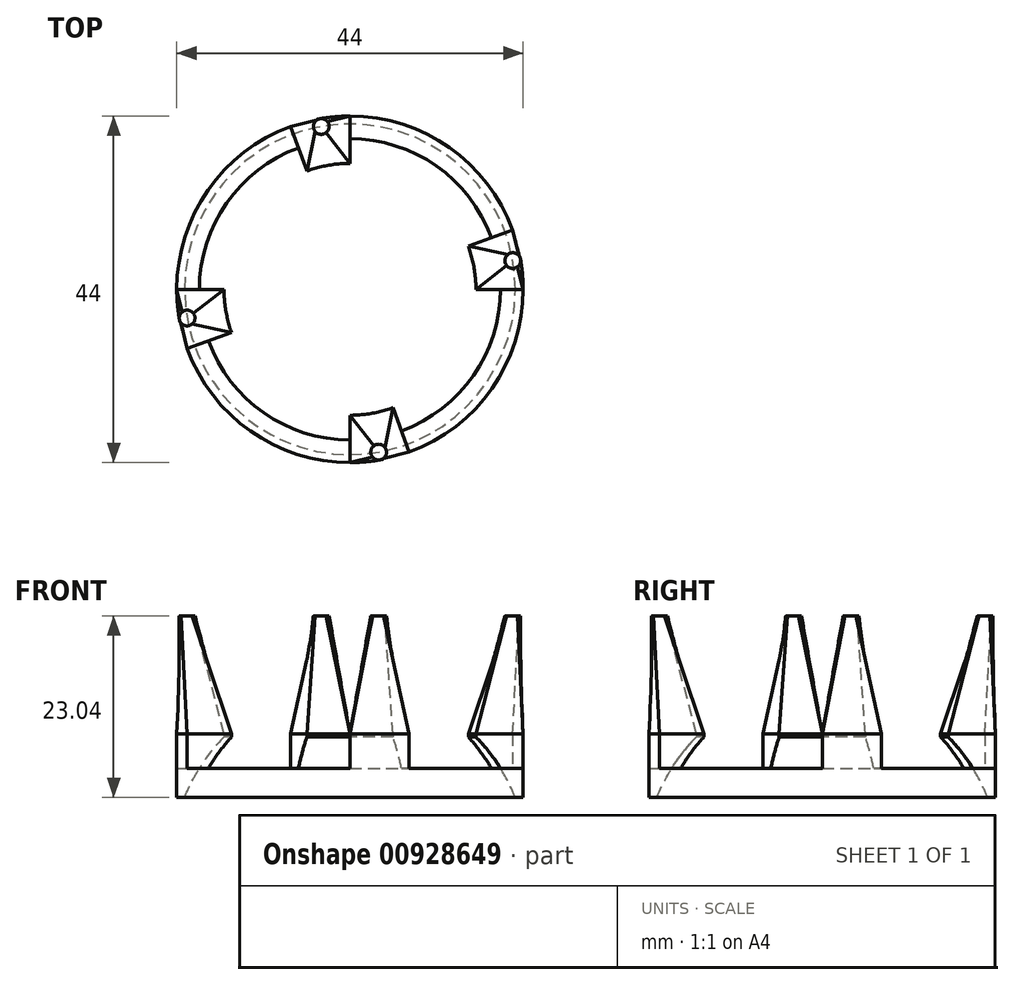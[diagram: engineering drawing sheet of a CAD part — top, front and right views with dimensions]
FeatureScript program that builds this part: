
annotation { "Feature Type Name" : "Feature", "Feature Type Description" : "" }
export const myFeature = defineFeature(function(context is Context, id is Id, definition is map)
    precondition{}
    {
        {
            var Q0;
            Q0=qCreatedBy(makeId("Front.planeOp"),FACE);
            var sketch = newSketch(context, id + "F0", { "sketchPlane" : qUnion([Q0])});
            skLineSegment(sketch, "E0", {"start": v(0, 0) * mm, "end": v(0, 52.54) * mm, "construction": true});
            skLineSegment(sketch, "E1.bottom", {"start": v(16, 0) * mm, "end": v(22, 0) * mm});
            skLineSegment(sketch, "E1.top", {"start": v(16, -8.04) * mm, "end": v(21, -8.04) * mm, "construction": true});
            skLineSegment(sketch, "E1.left", {"start": v(16, 0) * mm, "end": v(16, -0.37) * mm});
            skLineSegment(sketch, "E1.right", {"start": v(22, 0) * mm, "end": v(22, -8.04) * mm});
            skArc(sketch, "E2", {"start": v(16, -0.37) * mm, "mid": v(-20.5, -29.6) * mm, "end": v(21, -8.04) * mm, "construction": true});
            skArc(sketch, "E3", {"start": v(21, -8.04) * mm, "mid": v(18.88, -3.96) * mm, "end": v(16, -0.37) * mm});
            skLineSegment(sketch, "E4", {"start": v(21, -8.04) * mm, "end": v(22, -8.04) * mm});
            skLineSegment(sketch, "E5", {"start": v(16, -0.37) * mm, "end": v(16, -8.04) * mm, "construction": true});
            skPoint(sketch, "E6", {"position": v(19, 0) * mm});
            skSolve(sketch);
        }
        {
            var Q0;
            Q0 = qSketchRegion(id + "F0", true);
            var Q1;
            Q1=sQuery(id+"F0.wireOp",EDGE,"E0");
            revolve(context, id + "F1", {"surfaceOperationType" : NewSurfaceOperationType.NEW, "entities" : qUnion([Q0]), "axis" : qUnion([Q1]), "revolveType" : RevolveType.TWO_DIRECTIONS, "angle" : 20 * degree, "angleBack" : 0 * degree});
        }
        {
            var Q0;
            Q0=makeQuery(id+"F1.opRevolve","SWEPT_BODY",BODY,{"disambiguationData":[OSD([sQuery(id+"F0.wireOp",EDGE,"E1.bottom"),sQuery(id+"F0.wireOp",EDGE,"E1.left"),sQuery(id+"F0.wireOp",EDGE,"E1.right"),sQuery(id+"F0.wireOp",EDGE,"E3"),sQuery(id+"F0.wireOp",EDGE,"E4")])]});
            var Q1;
            Q1=sQuery(id+"F0.wireOp",EDGE,"E0");
            circularPattern(context, id + "F2", {"entities" : qUnion([Q0]), "axis" : qUnion([Q1]), "angle" : 360 * degree, "instanceCount" : 4, "equalSpace" : true});
        }
        {
            var Q0;
            Q0=makeQuery(id+"F1.opRevolve","CAP_FACE",FACE,{"disambiguationData":[OSD([sQuery(id+"F0.wireOp",EDGE,"E1.bottom"),sQuery(id+"F0.wireOp",EDGE,"E1.left"),sQuery(id+"F0.wireOp",EDGE,"E1.right"),sQuery(id+"F0.wireOp",EDGE,"E3"),sQuery(id+"F0.wireOp",EDGE,"E4")])],"isStart":false});
            var sketch = newSketch(context, id + "F3", { "sketchPlane" : qUnion([Q0])});
            skSolve(sketch);
        }
        {
            var Q0;
            Q0=makeQuery(id+"F3.imprint","IMPRINT",FACE,{"disambiguationData":[TD([[makeQuery(id+"F3.imprint","IMPRINT",EDGE,{"derivedFrom":makeQuery(id+"F1.opRevolve","CAP_EDGE",EDGE,{"disambiguationData":[OSD([sQuery(id+"F0.wireOp",EDGE,"E1.bottom")])],"isStart":false})}),1.0]])]});
            var sketch = newSketch(context, id + "F4", { "sketchPlane" : qUnion([Q0])});
            skArc(sketch, "E7.0", {"start": v(-21, -8.04) * mm, "mid": v(-20.15, -6.16) * mm, "end": v(-19.13, -4.35) * mm});
            skArc(sketch, "E8", {"start": v(-19.13, -4.35) * mm, "mid": v(-17.67, -2.27) * mm, "end": v(-16, -0.37) * mm, "construction": true});
            skLineSegment(sketch, "E9.0", {"start": v(-22, 0) * mm, "end": v(-22, -8.04) * mm, "construction": true});
            skLineSegment(sketch, "E10", {"start": v(-19.13, -4.35) * mm, "end": v(-22, -4.35) * mm});
            skLineSegment(sketch, "E11", {"start": v(-22, -4.35) * mm, "end": v(-22, -8.04) * mm});
            skLineSegment(sketch, "E12", {"start": v(-22, -8.04) * mm, "end": v(-22, -4.35) * mm});
            skSolve(sketch);
        }
        {
            var Q0;
            Q0=makeQuery(id+"F4.imprint","IMPRINT",FACE,{"disambiguationData":[TD([[makeQuery(id+"F4.imprint","IMPRINT",EDGE,{"derivedFrom":sQuery(id+"F4.wireOp",EDGE,"E7.0")}),1.0]])]});
            var Q1;
            Q1=sQuery(id+"F0.wireOp",EDGE,"E0");
            revolve(context, id + "F5", {"surfaceOperationType" : NewSurfaceOperationType.NEW, "entities" : qUnion([Q0]), "axis" : qUnion([Q1]), "revolveType" : RevolveType.FULL});
        }
        {
            var Q0;
            Q0=makeQuery(id+"F1.opRevolve","SWEPT_BODY",BODY,{"disambiguationData":[OSD([sQuery(id+"F0.wireOp",EDGE,"E1.bottom"),sQuery(id+"F0.wireOp",EDGE,"E1.left"),sQuery(id+"F0.wireOp",EDGE,"E1.right"),sQuery(id+"F0.wireOp",EDGE,"E3"),sQuery(id+"F0.wireOp",EDGE,"E4")])]});
            var Q1;
            Q1=makeQuery(id+"F2.opPattern","COPY",BODY,{"derivedFrom":makeQuery(id+"F1.opRevolve","SWEPT_BODY",BODY,{"disambiguationData":[OSD([sQuery(id+"F0.wireOp",EDGE,"E1.bottom"),sQuery(id+"F0.wireOp",EDGE,"E1.left"),sQuery(id+"F0.wireOp",EDGE,"E1.right"),sQuery(id+"F0.wireOp",EDGE,"E3"),sQuery(id+"F0.wireOp",EDGE,"E4")])]}),"instanceName":"1"});
            var Q2;
            Q2=makeQuery(id+"F2.opPattern","COPY",BODY,{"derivedFrom":makeQuery(id+"F1.opRevolve","SWEPT_BODY",BODY,{"disambiguationData":[OSD([sQuery(id+"F0.wireOp",EDGE,"E1.bottom"),sQuery(id+"F0.wireOp",EDGE,"E1.left"),sQuery(id+"F0.wireOp",EDGE,"E1.right"),sQuery(id+"F0.wireOp",EDGE,"E3"),sQuery(id+"F0.wireOp",EDGE,"E4")])]}),"instanceName":"2"});
            var Q3;
            Q3=makeQuery(id+"F2.opPattern","COPY",BODY,{"derivedFrom":makeQuery(id+"F1.opRevolve","SWEPT_BODY",BODY,{"disambiguationData":[OSD([sQuery(id+"F0.wireOp",EDGE,"E1.bottom"),sQuery(id+"F0.wireOp",EDGE,"E1.left"),sQuery(id+"F0.wireOp",EDGE,"E1.right"),sQuery(id+"F0.wireOp",EDGE,"E3"),sQuery(id+"F0.wireOp",EDGE,"E4")])]}),"instanceName":"3"});
            var Q4;
            Q4=makeQuery(id+"F4MRWHUxZCtjSTf_1.opRevolve","SWEPT_BODY",BODY,{"disambiguationData":[OSD([sQuery(id+"F4.wireOp",EDGE,"fbh8r7x2-dHDZ-tj1j-kEbG-0VAMOkKymPMU"),sQuery(id+"F4.wireOp",EDGE,"M89PfBS0-vETp-Bnr5-nqTN-LByxgd289nsR"),sQuery(id+"F4.wireOp",EDGE,"wZ66k8tc-VATU-Sq5I-3KXL-PqXNBZ8GxHJM")])]});
            var Q5;
            Q5=makeQuery(id+"F5.opRevolve","SWEPT_BODY",BODY,{"disambiguationData":[OSD([sQuery(id+"F0.wireOp",EDGE,"E4"),sQuery(id+"F4.wireOp",EDGE,"E7.0"),sQuery(id+"F4.wireOp",EDGE,"E10"),sQuery(id+"F4.wireOp",EDGE,"E12")])]});
            booleanBodies(context, id + "F6", {"operationType" : BooleanOperationType.UNION, "tools" : qUnion([Q0, Q1, Q2, Q3, Q4, Q5])});
        }
        {
            var Q0;
            Q0=makeQuery(id+"F1.opRevolve","SWEPT_FACE",FACE,{"disambiguationData":[OSD([sQuery(id+"F0.wireOp",EDGE,"E1.bottom")])]});
            var sketch = newSketch(context, id + "F7", { "sketchPlane" : qUnion([Q0])});
            skLineSegment(sketch, "E13.0", {"start": v(16, 0) * mm, "end": v(22, 0) * mm});
            skLineSegment(sketch, "E13.1", {"start": v(15.04, 5.47) * mm, "end": v(20.67, 7.52) * mm});
            skArc(sketch, "E13.2", {"start": v(20.67, 7.52) * mm, "mid": v(21.67, 3.82) * mm, "end": v(22, 0) * mm});
            skArc(sketch, "E13.3", {"start": v(15.04, 5.47) * mm, "mid": v(15.76, 2.78) * mm, "end": v(16, 0) * mm});
            skSolve(sketch);
        }
        {
            var Q0;
            Q0=makeQuery(id+"F7.imprint","IMPRINT",FACE,{"disambiguationData":[TD([[makeQuery(id+"F7.imprint","IMPRINT",EDGE,{"derivedFrom":sQuery(id+"F7.wireOp",EDGE,"E13.0")}),1.0]])]});
            cPlane(context, id + "F8", {"entities" : qUnion([Q0]), "cplaneType" : CPlaneType.OFFSET, "offset" : 15 * mm, "width" : 150 * mm, "height" : 150 * mm});
        }
        {
            var Q0;
            Q0=qCreatedBy(id+"F8.planeOp",FACE);
            var sketch = newSketch(context, id + "F9", { "sketchPlane" : qUnion([Q0])});
            skPoint(sketch, "E14.0", {"position": v(15.76, 2.78) * mm});
            skLineSegment(sketch, "E15", {"start": v(0, 0) * mm, "end": v(20.68, 3.65) * mm, "construction": true});
            skCircle(sketch, "E16", {"center": v(20.68, 3.65) * mm, "radius": 1 * mm});
            skPoint(sketch, "E17", {"position": v(19.86, 4.22) * mm});
            skPoint(sketch, "E18", {"position": v(21.5, 3.07) * mm});
            skLineSegment(sketch, "E19", {"start": v(19.86, 4.22) * mm, "end": v(21.5, 3.07) * mm, "construction": true});
            skLineSegment(sketch, "E20", {"start": v(21.25, 4.47) * mm, "end": v(20.1, 2.83) * mm, "construction": true});
            skLineSegment(sketch, "E21", {"start": v(20.1, 2.83) * mm, "end": v(19.86, 4.22) * mm, "construction": true});
            skPoint(sketch, "E22", {"position": v(19.98, 3.52) * mm});
            skSolve(sketch);
        }
        {
            var Q1;
            Q1=makeQuery(id+"F7.imprint","IMPRINT",FACE,{"disambiguationData":[TD([[makeQuery(id+"F7.imprint","IMPRINT",EDGE,{"derivedFrom":sQuery(id+"F7.wireOp",EDGE,"E13.0")}),1.0]])]});
            var Q2;
            Q2=makeQuery(id+"F9.imprint","IMPRINT",FACE,{"disambiguationData":[TD([[makeQuery(id+"F9.imprint","IMPRINT",EDGE,{"derivedFrom":sQuery(id+"F9.wireOp",EDGE,"E16")}),1.0]])]});
            loft(context, id + "F10", {"sheetProfilesArray" : [{ "sheetProfileEntities" : qUnion([Q1]) }, { "sheetProfileEntities" : qUnion([Q2]) }]});
        }
        {
            var Q0;
            Q0=makeQuery(id+"F10.opLoft","SWEPT_BODY",BODY,{"disambiguationData":[OSD([makeQuery(id+"F7.imprint","IMPRINT",FACE,{"disambiguationData":[TD([[makeQuery(id+"F7.imprint","IMPRINT",EDGE,{"derivedFrom":sQuery(id+"F7.wireOp",EDGE,"E13.0")}),1.0]])]}),makeQuery(id+"F9.imprint","IMPRINT",FACE,{"disambiguationData":[TD([[makeQuery(id+"F9.imprint","IMPRINT",EDGE,{"derivedFrom":sQuery(id+"F9.wireOp",EDGE,"E16")}),1.0]])]})])]});
            var Q1;
            Q1=sQuery(id+"F0.wireOp",EDGE,"E0");
            circularPattern(context, id + "F11", {"entities" : qUnion([Q0]), "axis" : qUnion([Q1]), "angle" : 360 * degree, "instanceCount" : 4, "equalSpace" : true});
        }
        {
            var Q0;
            Q0=makeQuery(id+"F1.opRevolve","SWEPT_BODY",BODY,{"disambiguationData":[OSD([sQuery(id+"F0.wireOp",EDGE,"E1.bottom"),sQuery(id+"F0.wireOp",EDGE,"E1.left"),sQuery(id+"F0.wireOp",EDGE,"E1.right"),sQuery(id+"F0.wireOp",EDGE,"E3"),sQuery(id+"F0.wireOp",EDGE,"E4")])]});
            var Q1;
            Q1=makeQuery(id+"F10.opLoft","SWEPT_BODY",BODY,{"disambiguationData":[OSD([makeQuery(id+"F7.imprint","IMPRINT",FACE,{"disambiguationData":[TD([[makeQuery(id+"F7.imprint","IMPRINT",EDGE,{"derivedFrom":sQuery(id+"F7.wireOp",EDGE,"E13.0")}),1.0]])]}),makeQuery(id+"F9.imprint","IMPRINT",FACE,{"disambiguationData":[TD([[makeQuery(id+"F9.imprint","IMPRINT",EDGE,{"derivedFrom":sQuery(id+"F9.wireOp",EDGE,"E16")}),1.0]])]})])]});
            var Q2;
            Q2=makeQuery(id+"F11.opPattern","COPY",BODY,{"derivedFrom":makeQuery(id+"F10.opLoft","SWEPT_BODY",BODY,{"disambiguationData":[OSD([makeQuery(id+"F7.imprint","IMPRINT",FACE,{"disambiguationData":[TD([[makeQuery(id+"F7.imprint","IMPRINT",EDGE,{"derivedFrom":sQuery(id+"F7.wireOp",EDGE,"E13.0")}),1.0]])]}),makeQuery(id+"F9.imprint","IMPRINT",FACE,{"disambiguationData":[TD([[makeQuery(id+"F9.imprint","IMPRINT",EDGE,{"derivedFrom":sQuery(id+"F9.wireOp",EDGE,"E16")}),1.0]])]})])]}),"instanceName":"1"});
            var Q3;
            Q3=makeQuery(id+"F11.opPattern","COPY",BODY,{"derivedFrom":makeQuery(id+"F10.opLoft","SWEPT_BODY",BODY,{"disambiguationData":[OSD([makeQuery(id+"F7.imprint","IMPRINT",FACE,{"disambiguationData":[TD([[makeQuery(id+"F7.imprint","IMPRINT",EDGE,{"derivedFrom":sQuery(id+"F7.wireOp",EDGE,"E13.0")}),1.0]])]}),makeQuery(id+"F9.imprint","IMPRINT",FACE,{"disambiguationData":[TD([[makeQuery(id+"F9.imprint","IMPRINT",EDGE,{"derivedFrom":sQuery(id+"F9.wireOp",EDGE,"E16")}),1.0]])]})])]}),"instanceName":"2"});
            var Q4;
            Q4=makeQuery(id+"F11.opPattern","COPY",BODY,{"derivedFrom":makeQuery(id+"F10.opLoft","SWEPT_BODY",BODY,{"disambiguationData":[OSD([makeQuery(id+"F7.imprint","IMPRINT",FACE,{"disambiguationData":[TD([[makeQuery(id+"F7.imprint","IMPRINT",EDGE,{"derivedFrom":sQuery(id+"F7.wireOp",EDGE,"E13.0")}),1.0]])]}),makeQuery(id+"F9.imprint","IMPRINT",FACE,{"disambiguationData":[TD([[makeQuery(id+"F9.imprint","IMPRINT",EDGE,{"derivedFrom":sQuery(id+"F9.wireOp",EDGE,"E16")}),1.0]])]})])]}),"instanceName":"3"});
            booleanBodies(context, id + "F12", {"operationType" : BooleanOperationType.UNION, "tools" : qUnion([Q0, Q1, Q2, Q3, Q4])});
        }
    });
